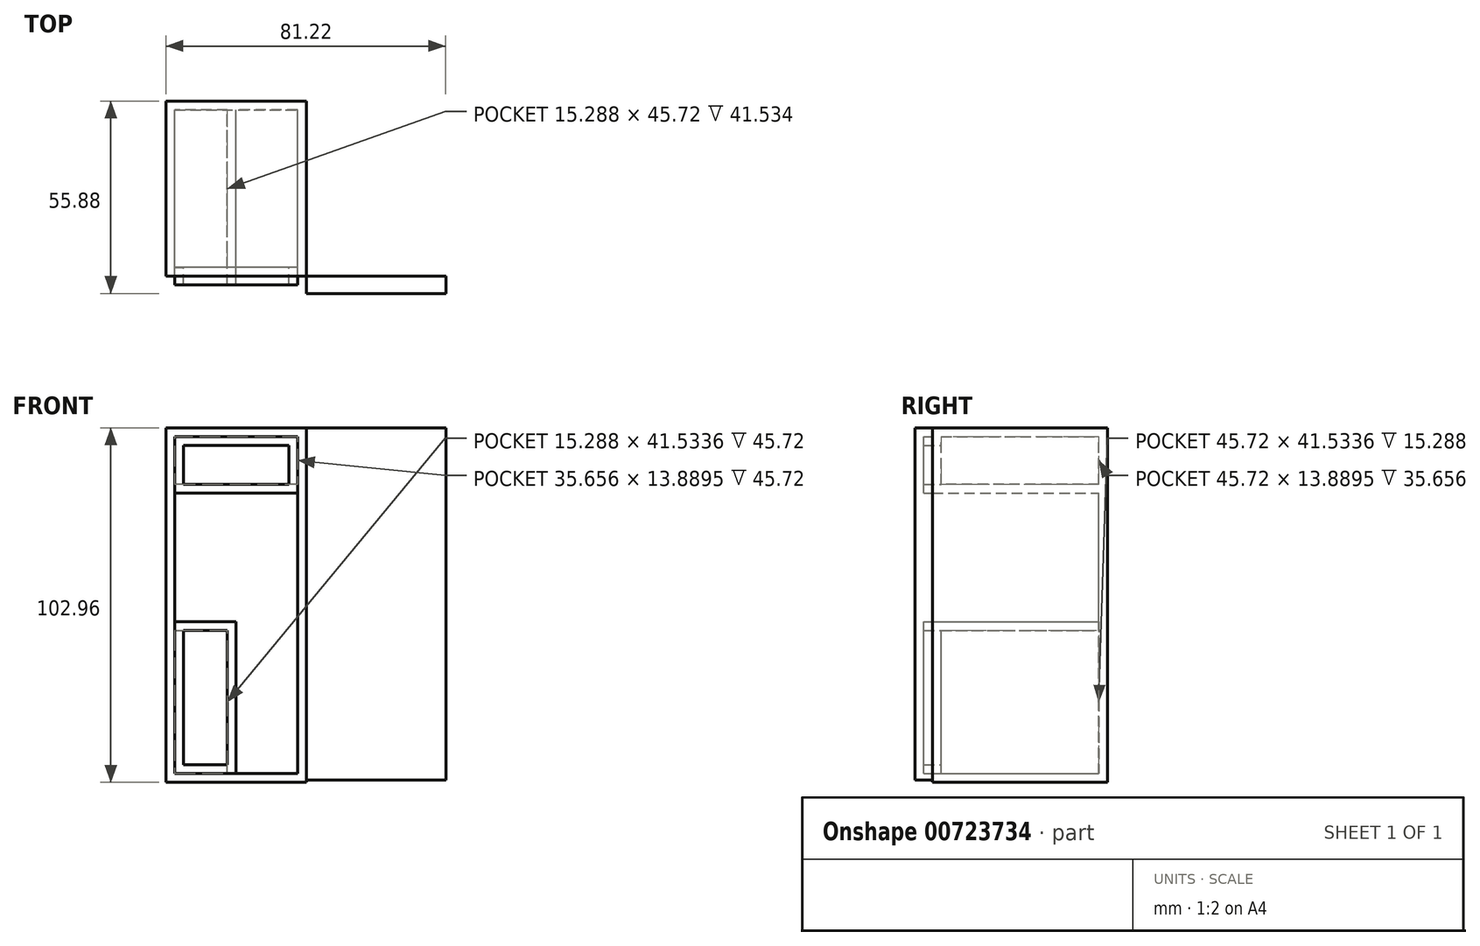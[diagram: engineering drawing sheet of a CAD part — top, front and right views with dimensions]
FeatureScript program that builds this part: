
annotation { "Feature Type Name" : "Feature", "Feature Type Description" : "" }
export const myFeature = defineFeature(function(context is Context, id is Id, definition is map)
    precondition{}
    {
        {
            var Q0;
            Q0=qCreatedBy(makeId("Front.planeOp"),FACE);
            var sketch = newSketch(context, id + "F0", { "sketchPlane" : qUnion([Q0])});
            skLineSegment(sketch, "E0.bottom", {"start": v(-35.4, 1.96) * mm, "end": v(-76.14, 1.96) * mm});
            skLineSegment(sketch, "E0.top", {"start": v(-35.4, 104.92) * mm, "end": v(-76.14, 104.92) * mm});
            skLineSegment(sketch, "E0.left", {"start": v(-35.4, 1.96) * mm, "end": v(-35.4, 104.92) * mm});
            skLineSegment(sketch, "E0.right", {"start": v(-76.14, 1.96) * mm, "end": v(-76.14, 104.92) * mm});
            skPoint(sketch, "E0.middle", {"position": v(-55.78, 53.44) * mm});
            skSolve(sketch);
        }
        {
            var Q0;
            Q0=makeQuery(id+"F0.imprint","IMPRINT",FACE,{"disambiguationData":[TD([[makeQuery(id+"F0.imprint","IMPRINT",EDGE,{"derivedFrom":sQuery(id+"F0.wireOp",EDGE,"E0.bottom")}),-1.0]])]});
            extrude(context, id + "F1", {"entities" : qUnion([Q0]), "depth" : 25.4 * mm, "offsetDistance" : 25.4 * mm});
        }
        {
            var Q0;
            Q0=makeQuery(id+"F1.opExtrude","CAP_FACE",FACE,{"disambiguationData":[OSD([sQuery(id+"F0.wireOp",EDGE,"E0.bottom"),sQuery(id+"F0.wireOp",EDGE,"E0.top"),sQuery(id+"F0.wireOp",EDGE,"E0.left"),sQuery(id+"F0.wireOp",EDGE,"E0.right")])],"isStart":false});
            extrude(context, id + "F2", {"entities" : qUnion([Q0]), "operationType" : NewBodyOperationType.ADD, "depth" : 25.4 * mm, "offsetDistance" : 25.4 * mm});
        }
        {
            var Q0;
            Q0=makeQuery(id+"F2.opExtrude","CAP_FACE",FACE,{"disambiguationData":[OSD([sQuery(id+"F0.wireOp",EDGE,"E0.bottom"),sQuery(id+"F0.wireOp",EDGE,"E0.top"),sQuery(id+"F0.wireOp",EDGE,"E0.left"),sQuery(id+"F0.wireOp",EDGE,"E0.right")])],"isStart":false});
            shell(context, id + "F3", {"entities" : qUnion([Q0]), "thickness" : 2.54 * mm});
        }
        {
            var Q0;
            Q0=makeQuery(id+"F2.opExtrude","CAP_FACE",FACE,{"disambiguationData":[OSD([sQuery(id+"F0.wireOp",EDGE,"E0.bottom"),sQuery(id+"F0.wireOp",EDGE,"E0.top"),sQuery(id+"F0.wireOp",EDGE,"E0.left"),sQuery(id+"F0.wireOp",EDGE,"E0.right")])],"isStart":false});
            var sketch = newSketch(context, id + "F4", { "sketchPlane" : qUnion([Q0])});
            skLineSegment(sketch, "E1.bottom", {"start": v(-35.4, 104.92) * mm, "end": v(5.08, 104.92) * mm});
            skLineSegment(sketch, "E1.top", {"start": v(-35.4, 2.68) * mm, "end": v(5.08, 2.68) * mm});
            skLineSegment(sketch, "E1.left", {"start": v(-35.4, 104.92) * mm, "end": v(-35.4, 2.68) * mm});
            skLineSegment(sketch, "E1.right", {"start": v(5.08, 104.92) * mm, "end": v(5.08, 2.68) * mm});
            skSolve(sketch);
        }
        {
            var Q0;
            Q0=makeQuery(id+"F4.imprint","IMPRINT",FACE,{"disambiguationData":[TD([[makeQuery(id+"F4.imprint","IMPRINT",EDGE,{"derivedFrom":sQuery(id+"F4.wireOp",EDGE,"E1.bottom")}),-1.0]])]});
            extrude(context, id + "F5", {"entities" : qUnion([Q0]), "depth" : 5.08 * mm, "offsetDistance" : 25.4 * mm});
        }
        {
            var Q0;
            Q0=makeQuery(id+"F3.opShell","OFFSET_FACE",FACE,{"disambiguationData":[OSD([sQuery(id+"F0.wireOp",EDGE,"E0.bottom"),sQuery(id+"F0.wireOp",EDGE,"E0.top"),sQuery(id+"F0.wireOp",EDGE,"E0.left"),sQuery(id+"F0.wireOp",EDGE,"E0.right")])]});
            var sketch = newSketch(context, id + "F6", { "sketchPlane" : qUnion([Q0])});
            skLineSegment(sketch, "E2.bottom", {"start": v(-73.6, 102.38) * mm, "end": v(-37.95, 102.38) * mm});
            skLineSegment(sketch, "E2.top", {"start": v(-73.6, 85.95) * mm, "end": v(-37.95, 85.95) * mm});
            skLineSegment(sketch, "E2.left", {"start": v(-73.6, 102.38) * mm, "end": v(-73.6, 85.95) * mm});
            skLineSegment(sketch, "E2.right", {"start": v(-37.95, 102.38) * mm, "end": v(-37.95, 85.95) * mm});
            skLineSegment(sketch, "E3.bottom", {"start": v(-73.6, 48.58) * mm, "end": v(-55.78, 48.58) * mm});
            skLineSegment(sketch, "E3.top", {"start": v(-73.6, 4.5) * mm, "end": v(-55.78, 4.5) * mm});
            skLineSegment(sketch, "E3.left", {"start": v(-73.6, 48.58) * mm, "end": v(-73.6, 4.5) * mm});
            skLineSegment(sketch, "E3.right", {"start": v(-55.78, 48.58) * mm, "end": v(-55.78, 4.5) * mm});
            skSolve(sketch);
        }
        {
            var Q0;
            Q0=makeQuery(id+"F6.imprint","IMPRINT",FACE,{"disambiguationData":[TD([[makeQuery(id+"F6.imprint","IMPRINT",EDGE,{"derivedFrom":sQuery(id+"F6.wireOp",EDGE,"E2.bottom")}),1.0]])]});
            var Q1;
            Q1=makeQuery(id+"F6.imprint","IMPRINT",FACE,{"disambiguationData":[TD([[makeQuery(id+"F6.imprint","IMPRINT",EDGE,{"derivedFrom":sQuery(id+"F6.wireOp",EDGE,"E3.bottom")}),-1.0]])]});
            extrude(context, id + "F7", {"entities" : qUnion([Q0, Q1]), "operationType" : NewBodyOperationType.ADD, "depth" : 50.8 * mm, "offsetDistance" : 25.4 * mm});
        }
        {
            var Q0;
            Q0=makeQuery(id+"F7.opExtrude","CAP_FACE",FACE,{"disambiguationData":[OSD([sQuery(id+"F6.wireOp",EDGE,"E2.bottom"),sQuery(id+"F6.wireOp",EDGE,"E2.top"),sQuery(id+"F6.wireOp",EDGE,"E2.left"),sQuery(id+"F6.wireOp",EDGE,"E2.right")])],"isStart":false});
            var Q1;
            Q1=makeQuery(id+"F7.opExtrude","CAP_FACE",FACE,{"disambiguationData":[OSD([sQuery(id+"F6.wireOp",EDGE,"E3.bottom"),sQuery(id+"F6.wireOp",EDGE,"E3.top"),sQuery(id+"F6.wireOp",EDGE,"E3.left"),sQuery(id+"F6.wireOp",EDGE,"E3.right")])],"isStart":false});
            shell(context, id + "F8", {"entities" : qUnion([Q0, Q1]), "thickness" : 2.54 * mm});
        }
    });
